# Revit family: 483260001(1)
name_source: partatom
category: Generic Models
units: mm (PartAtom-declared; Revit-internal decimal feet)

## family parameters
Always vertical = Yes
Can host rebar = No
Cut with Voids When Loaded = No
Host = Floor
Room Calculation Point = No
Shared = Yes

## types (1)
- 483260001
    ARTICLENO = NB
    BEZ = Afvoerrooster geschikt voor pot 50-60 mm, Ø 93 mm buitenzijde rooster
    BOMINFO = LINA
    CATALOG = König & Ronneberger
    CNSORDERNO = 483260001
    D1 = 93 mm  [stored 0.305118 ft]
    D2 = 64 mm  [stored 0.209974 ft]
    Description = Balcony transit and drain wastes
    H = 15 mm  [stored 0.0492126 ft]
    HTML = Product page
    INFO = PDF Catalog
    LINA = 483260001
    LODLEVEL = 300
    Manufacturer = KOERO
    Model = 483260001
    NB = 483260001(1)
    NBSYN = $CNSORDERNO.($LODLEVEL.)
    NN = PLUVETTA® ROOSTER
    NT = Balcony transit and drain wastes
    SUPPLIER = KOERO

note: [stored X ft] marks values corroborated as IEEE doubles in the binary element streams (Revit-internal decimal feet)

## geometry (parser evidence)
native form markers: Sweep x4
no freeform markers — native parametric forms only
